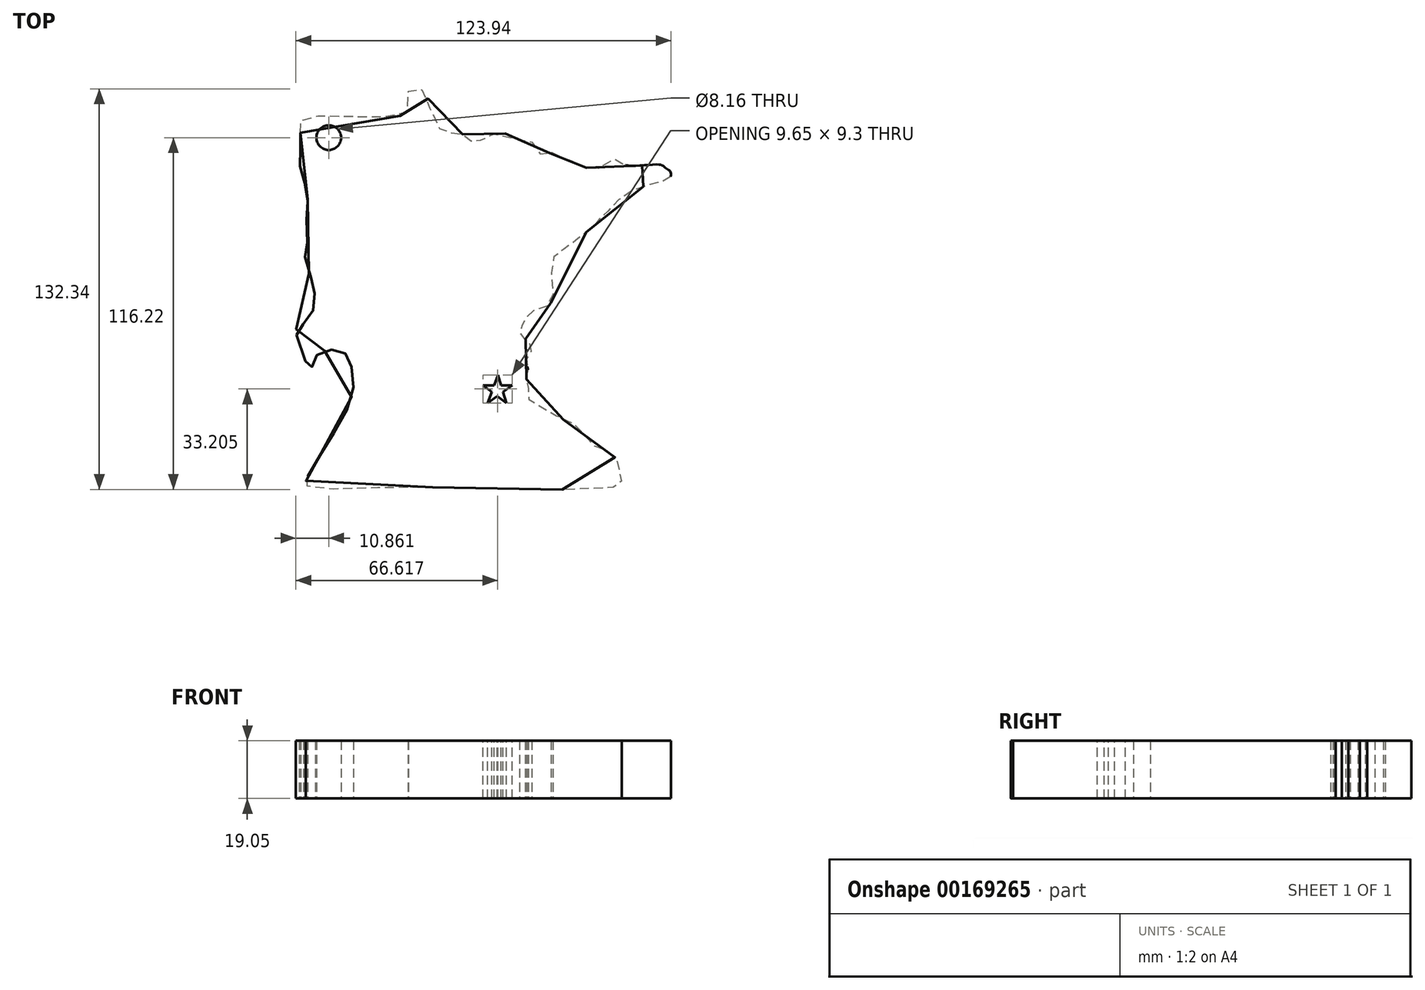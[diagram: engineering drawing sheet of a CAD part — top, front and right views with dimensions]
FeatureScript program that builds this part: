
annotation { "Feature Type Name" : "Feature", "Feature Type Description" : "" }
export const myFeature = defineFeature(function(context is Context, id is Id, definition is map)
    precondition{}
    {
        {
            var Q0;
            Q0=qCreatedBy(makeId("Top.planeOp"),FACE);
            var sketch = newSketch(context, id + "F0", { "sketchPlane" : qUnion([Q0])});
            skFitSpline(sketch, "E0", {"points": [v(-45.42, 57.98) * mm, v(-44.29, 59.59) * mm, v(-45.14, 61.1) * mm, v(-44.67, 63.57) * mm, v(-43.34, 63.76) * mm, v(-11.6, 63.76) * mm, v(-10.66, 64.42) * mm, v(-9.8, 65.27) * mm, v(-9.8, 71.34) * mm, v(-9.05, 72.1) * mm, v(-6.59, 72.47) * mm, v(-4.6, 71.9) * mm, v(-3.37, 69.91) * mm, v(-0.9, 60.16) * mm, v(0.7, 59.4) * mm, v(1.56, 59.02) * mm, v(3.64, 58.07) * mm, v(5.35, 57.79) * mm, v(6.49, 57.22) * mm, v(7.62, 57.5) * mm, v(9.23, 56.84) * mm, v(10.37, 55.23) * mm, v(11.13, 55.23) * mm, v(12.93, 54.85) * mm, v(13.5, 55.52) * mm, v(14.06, 55.52) * mm, v(15.3, 55.42) * mm, v(17.28, 57.13) * mm, v(23.73, 57.32) * mm, v(26.95, 55.42) * mm, v(30.26, 55.42) * mm, v(31.68, 54) * mm, v(32.91, 51.82) * mm, v(34.43, 50.78) * mm, v(36.42, 51.06) * mm, v(37.37, 51.35) * mm, v(38.4, 51.63) * mm, v(39.92, 51.16) * mm, v(41.25, 49.64) * mm, v(43.43, 48.89) * mm, v(45.04, 48.5) * mm, v(46.18, 46.9) * mm, v(47.5, 46.52) * mm, v(48.92, 46.42) * mm, v(50.15, 45.85) * mm, v(53.1, 46.23) * mm, v(56.6, 48.03) * mm, v(58.77, 49.45) * mm, v(60.48, 48.8) * mm, v(61.71, 47.37) * mm, v(73.27, 47.46) * mm, v(74.69, 46.8) * mm, v(76.1, 45.76) * mm, v(76.87, 45.2) * mm, v(76.96, 43.4) * mm, v(74.97, 42.16) * mm, v(67.87, 40.17) * mm, v(60.95, 36.86) * mm, v(55.84, 31.65) * mm, v(53.23, 29.25) * mm, v(51.93, 27.42) * mm, v(49.3, 25.27) * mm, v(45.6, 22.4) * mm, v(40.3, 18.6) * mm, v(37.61, 15.07) * mm, v(37.85, 2.96) * mm, v(34.45, 0) * mm, v(29.73, -1.88) * mm, v(29.14, -4.08) * mm, v(27.53, -5.93) * mm, v(27.1, -7.9) * mm, v(27.94, -9.63) * mm, v(29.08, -10.11) * mm, v(29.97, -10.83) * mm, v(31.05, -13.26) * mm, v(30.13, -15.39) * mm, v(29.2, -17.44) * mm, v(29.56, -19.22) * mm, v(29.77, -20.57) * mm, v(29.14, -21) * mm, v(29.2, -23.26) * mm, v(29.7, -24.11) * mm, v(29.85, -27.45) * mm, v(29.7, -29.01) * mm, v(32.05, -31.92) * mm, v(37.86, -34.12) * mm, v(39.5, -35.68) * mm, v(45.6, -38.52) * mm, v(47.09, -40) * mm, v(49.93, -43.7) * mm, v(52.62, -45.97) * mm, v(55.68, -46.82) * mm, v(58.8, -49.59) * mm, v(60.76, -56.57) * mm, v(59.8, -58.9) * mm, v(57.15, -59.12) * mm, v(47.79, -59.76) * mm, v(29.71, -59.65) * mm, v(15.57, -59.55) * mm, v(0, -59.23) * mm, v(-17.81, -59.23) * mm, v(-42.48, -59.12) * mm, v(-43.54, -57.95) * mm, v(-43.22, -56.04) * mm, v(-39.4, -49.34) * mm, v(-34.08, -40.94) * mm, v(-29.4, -32.22) * mm, v(-27.8, -24.99) * mm, v(-28.44, -19.35) * mm, v(-29.4, -16.06) * mm, v(-31.74, -14.25) * mm, v(-34.82, -13.72) * mm, v(-38.01, -14.25) * mm, v(-40.78, -16.8) * mm, v(-41.2, -19.35) * mm, v(-42.27, -19.04) * mm, v(-43.12, -18.82) * mm, v(-43.86, -17.02) * mm, v(-46.84, -7.34) * mm, v(-45.78, -6.06) * mm, v(-42.8, -3.73) * mm, v(-41, 0) * mm, v(-40.75, 4.13) * mm, v(-40.51, 7.35) * mm, v(-43.02, 12.36) * mm, v(-43.74, 18.45) * mm, v(-43.14, 20.84) * mm, v(-43.38, 27.4) * mm, v(-43.14, 33.37) * mm, v(-43.02, 37.3) * mm, v(-44.3, 42.72) * mm, v(-45.4, 46.55) * mm, v(-45.73, 50.05) * mm, v(-45.27, 55.5) * mm, v(-45.42, 57.98) * mm]});
            skCircle(sketch, "E1", {"center": v(-35.98, 56.35) * mm, "radius": 4.08 * mm});
            skSolve(sketch);
        }
        {
            var Q0;
            Q0=makeQuery(id+"F0.imprint","IMPRINT",FACE,{"disambiguationData":[TD([[makeQuery(id+"F0.imprint","IMPRINT",EDGE,{"derivedFrom":sQuery(id+"F0.wireOp",EDGE,"E0")}),-1.0]])]});
            var Q1;
            Q1=sQuery(id+"F0.wireOp",EDGE,"E0");
            extrude(context, id + "F1", {"entities" : qUnion([Q0]), "surfaceEntities" : qUnion([Q1]), "depth" : 19.05 * mm});
        }
        {
            var Q0;
            Q0=makeQuery(id+"F1.opExtrude","CAP_FACE",FACE,{"disambiguationData":[OSD([sQuery(id+"F0.wireOp",EDGE,"E0"),sQuery(id+"F0.wireOp",EDGE,"E1")])],"isStart":false});
            var sketch = newSketch(context, id + "F2", { "sketchPlane" : qUnion([Q0])});
            skLineSegment(sketch, "E2", {"start": v(16.53, -31.31) * mm, "end": v(17.84, -27.66) * mm});
            skLineSegment(sketch, "E3", {"start": v(19.86, -22.02) * mm, "end": v(20.96, -25.53) * mm});
            skLineSegment(sketch, "E4", {"start": v(22.77, -31.31) * mm, "end": v(19.7, -29.04) * mm});
            skLineSegment(sketch, "E5", {"start": v(14.95, -25.53) * mm, "end": v(18.6, -25.53) * mm});
            skLineSegment(sketch, "E6", {"start": v(24.6, -25.53) * mm, "end": v(21.63, -27.66) * mm});
            skLineSegment(sketch, "E7.trimOffspring", {"start": v(18.6, -25.53) * mm, "end": v(19.86, -22.02) * mm});
            skLineSegment(sketch, "E8.trimOffspring", {"start": v(20.96, -25.53) * mm, "end": v(24.6, -25.53) * mm});
            skLineSegment(sketch, "E9.trimOffspring", {"start": v(21.63, -27.66) * mm, "end": v(22.77, -31.31) * mm});
            skLineSegment(sketch, "E10.trimOffspring", {"start": v(19.7, -29.04) * mm, "end": v(16.53, -31.31) * mm});
            skLineSegment(sketch, "E11.trimOffspring", {"start": v(17.84, -27.66) * mm, "end": v(14.95, -25.53) * mm});
            skSolve(sketch);
        }
        {
            var Q0;
            Q0 = qSketchRegion(id + "F2", true);
            extrude(context, id + "F3", {"entities" : qUnion([Q0]), "operationType" : NewBodyOperationType.REMOVE, "oppositeDirection" : true, "depth" : 25.4 * mm});
        }
    });
